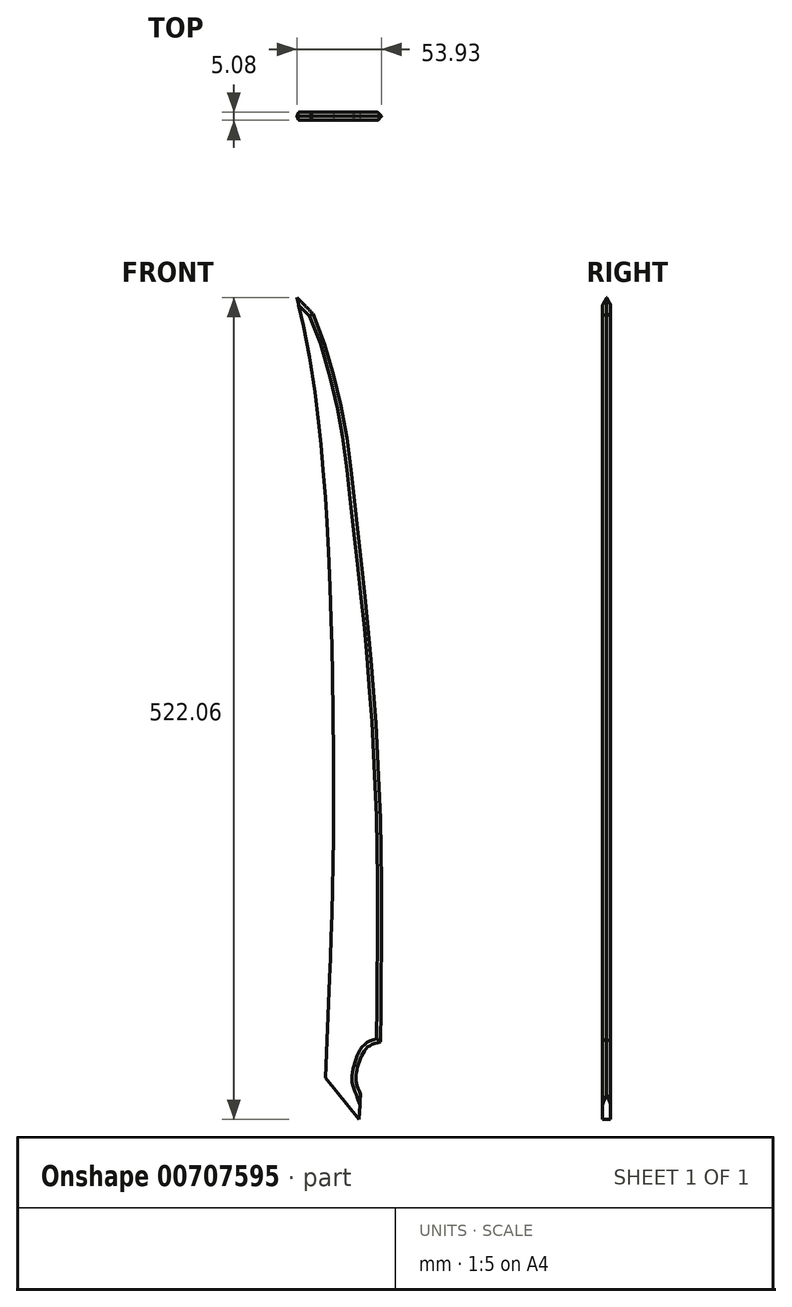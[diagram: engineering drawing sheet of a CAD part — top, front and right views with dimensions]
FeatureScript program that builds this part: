
annotation { "Feature Type Name" : "Feature", "Feature Type Description" : "" }
export const myFeature = defineFeature(function(context is Context, id is Id, definition is map)
    precondition{}
    {
        {
            var Q0;
            Q0=qCreatedBy(makeId("Front.planeOp"),FACE);
            var sketch = newSketch(context, id + "F0", { "sketchPlane" : qUnion([Q0])});
            skLineSegment(sketch, "E0", {"start": v(11.7, 8.56) * mm, "end": v(10.7, -7.18) * mm});
            skLineSegment(sketch, "E1", {"start": v(10.7, -7.18) * mm, "end": v(-10.6, 19) * mm});
            skLineSegment(sketch, "E2", {"start": v(-10.6, 19) * mm, "end": v(-7.8, 82.36) * mm});
            skFitSpline(sketch, "E3", {"points": [v(-7.8, 82.36) * mm, v(-7.24, 98.94) * mm, v(-6.59, 117.12) * mm, v(-5.83, 142.02) * mm, v(-5.45, 168.32) * mm, v(-5.52, 230.34) * mm, v(-6.26, 285.7) * mm, v(-7.2, 315.28) * mm, v(-8.95, 361.43) * mm, v(-10.4, 387.63) * mm, v(-13, 416.84) * mm, v(-15.01, 437.7) * mm, v(-21.29, 480.96) * mm, v(-27.2, 508.68) * mm, v(-28.7, 514.88) * mm], "startDerivative": vector(10.22, 308.11) * mm, "endDerivative": vector(-37.95, 155.7) * mm});
            skLineSegment(sketch, "E4", {"start": v(-28.7, 514.88) * mm, "end": v(-18.5, 504.49) * mm});
            skFitSpline(sketch, "E5", {"points": [v(-18.5, 504.49) * mm, v(-14.2, 494.72) * mm, v(-10.4, 483.17) * mm, v(-6.54, 469.9) * mm, v(-3.1, 457.05) * mm, v(-0.51, 445.6) * mm, v(1.47, 435.93) * mm, v(2.96, 426.2) * mm, v(4.35, 415.6) * mm, v(5.85, 403.15) * mm, v(7.18, 390.92) * mm, v(9.67, 369.53) * mm, v(11.56, 352.56) * mm, v(15.2, 318.42) * mm, v(18.03, 290.8) * mm, v(19.92, 265.34) * mm, v(21.72, 242.6) * mm, v(22.69, 220.79) * mm, v(23.65, 203.25) * mm, v(24.47, 178.85) * mm, v(25.08, 148.77) * mm, v(25.19, 106.94) * mm, v(24.82, 74.57) * mm, v(24.5, 42) * mm], "startDerivative": vector(138.63, -295.52) * mm, "endDerivative": vector(-5.12, -584.15) * mm});
            skFitSpline(sketch, "E6", {"points": [v(24.5, 42) * mm, v(16.7, 39) * mm, v(12.5, 33.24) * mm, v(9.61, 24.95) * mm, v(8.9, 16.91) * mm, v(10.33, 12.23) * mm, v(11.7, 8.56) * mm], "startDerivative": vector(-46.28, -12) * mm, "endDerivative": vector(10.21, -28.51) * mm});
            skFitSpline(sketch, "E7", {"points": [v(-10.6, 84.98) * mm, v(-8.5, 83) * mm, v(-6.65, 78.8) * mm, v(-5.89, 72.07) * mm, v(-5.76, 61.33) * mm, v(-5.64, 47.1) * mm, v(-5.9, 35.6) * mm, v(-6.47, 31.43) * mm, v(-6.34, 26.97) * mm, v(-4.57, 21.8) * mm, v(-2.21, 17.83) * mm, v(0, 15.05) * mm, v(2.28, 13.08) * mm, v(5.76, 11.32) * mm, v(8.69, 10.16) * mm, v(11.04, 8.9) * mm, v(12.38, 7.6) * mm, v(13.09, 5.99) * mm, v(12.89, 2.76) * mm, v(12.15, -3.9) * mm, v(11.7, -8.74) * mm, v(11.08, -13.22) * mm], "startDerivative": vector(59.9, -45.86) * mm, "endDerivative": vector(-14.62, -97.53) * mm});
            skLineSegment(sketch, "E8", {"start": v(11.08, -13.22) * mm, "end": v(11.08, -15.97) * mm});
            skLineSegment(sketch, "E9", {"start": v(11.08, -15.97) * mm, "end": v(-11.03, -15.97) * mm});
            skLineSegment(sketch, "E10", {"start": v(-11.03, -15.97) * mm, "end": v(-11.2, -13.29) * mm});
            skFitSpline(sketch, "E11", {"points": [v(-11.2, -13.29) * mm, v(-11.2, -11.84) * mm, v(-11.2, -5.52) * mm, v(-11.51, 1.49) * mm, v(-12.16, 4.66) * mm, v(-13.4, 9.05) * mm, v(-15.15, 13.55) * mm, v(-16.64, 17.33) * mm, v(-19.12, 23.61) * mm, v(-19.55, 26.56) * mm, v(-18.64, 31.28) * mm, v(-16.79, 35.33) * mm, v(-14.77, 40.57) * mm, v(-13.5, 46.17) * mm, v(-12.6, 53.4) * mm, v(-12.2, 59.96) * mm, v(-12.37, 65.97) * mm, v(-12.16, 73.91) * mm, v(-11.5, 81.04) * mm, v(-11.2, 84.64) * mm, v(-10.6, 84.98) * mm], "startDerivative": vector(-0.12, 43.3) * mm, "endDerivative": vector(35.61, 8.6) * mm});
            skFitSpline(sketch, "E12", {"points": [v(11.08, -13.22) * mm, v(15.57, -17.52) * mm, v(22.06, -24.41) * mm, v(29.6, -33.47) * mm, v(35.84, -41.56) * mm, v(40.17, -47.64) * mm, v(44.57, -55.74) * mm, v(47.94, -62.06) * mm, v(51.06, -67.51) * mm, v(52.42, -69.67) * mm, v(49.81, -81.38) * mm, v(45.5, -94.07) * mm, v(41.24, -106.63) * mm, v(36.2, -120.43) * mm, v(32.84, -130.03) * mm, v(29.35, -138.2) * mm, v(27.78, -142.23) * mm, v(23.27, -152.08) * mm, v(21.3, -154.75) * mm, v(16.02, -157.43) * mm, v(8.58, -160.03) * mm, v(4.77, -160.41) * mm, v(4.83, -154.75) * mm, v(8.26, -152.78) * mm, v(13.03, -150.3) * mm, v(16.97, -147.44) * mm, v(20.66, -141.85) * mm, v(25.37, -129.07) * mm, v(31.66, -108.36) * mm, v(36.51, -89.69) * mm, v(39.56, -77.02) * mm, v(39.75, -72.83) * mm, v(38.74, -67.42) * mm, v(35.21, -61.22) * mm, v(28.26, -50.55) * mm, v(23.02, -43.89) * mm, v(18.43, -38.21) * mm, v(13.22, -32.69) * mm, v(7.93, -27.32) * mm, v(6.6, -20.94) * mm, v(11.08, -13.22) * mm]});
            skLineSegment(sketch, "E13.bottom", {"start": v(-12.44, -13.29) * mm, "end": v(11.54, -13.29) * mm});
            skLineSegment(sketch, "E13.top", {"start": v(-12.44, -29.01) * mm, "end": v(11.54, -29.01) * mm});
            skLineSegment(sketch, "E13.left", {"start": v(-12.44, -13.29) * mm, "end": v(-12.44, -29.01) * mm});
            skLineSegment(sketch, "E13.right", {"start": v(11.54, -13.29) * mm, "end": v(11.54, -29.01) * mm});
            skLineSegment(sketch, "E14", {"start": v(0, -32.56) * mm, "end": v(0, -38.28) * mm});
            skFitSpline(sketch, "E15", {"points": [v(-10.75, -28.03) * mm, v(-9.93, -35.6) * mm, v(-9.25, -45.2) * mm, v(-8.25, -64.06) * mm, v(-7.6, -83.45) * mm, v(-7.55, -95.02) * mm, v(-7.45, -109.5) * mm, v(-7.73, -122.65) * mm, v(-8.29, -138.57) * mm, v(-9.14, -152.56) * mm, v(-9.03, -155.04) * mm], "startDerivative": vector(11.05, -94.6) * mm, "endDerivative": vector(4.37, -43.01) * mm});
            skLineSegment(sketch, "E16", {"start": v(-9.9, -153.6) * mm, "end": v(9.57, -153.6) * mm});
            skFitSpline(sketch, "E17.MirrorCS", {"points": [v(10.75, -28.03) * mm, v(9.93, -35.6) * mm, v(9.25, -45.2) * mm, v(8.25, -64.06) * mm, v(7.6, -83.45) * mm, v(7.55, -95.02) * mm, v(7.45, -109.5) * mm, v(7.73, -122.65) * mm, v(8.29, -138.57) * mm, v(9.14, -152.56) * mm, v(9.03, -155.04) * mm], "startDerivative": vector(-11.05, -94.6) * mm, "endDerivative": vector(-4.37, -43.01) * mm});
            skSolve(sketch);
        }
        {
            var Q0;
            {var subQ0=sQuery(id+"F0.wireOp",EDGE,"E3");Q0=makeQuery(id+"F0.imprint","IMPRINT",FACE,{"disambiguationData":[TD([[makeQuery(id+"F0.imprint","IMPRINT",EDGE,{"derivedFrom":subQ0}),-1.0]])]});}
            var Q1;
            {var subQ0=sQuery(id+"F0.wireOp",EDGE,"E1");Q1=makeQuery(id+"F0.imprint","IMPRINT",FACE,{"disambiguationData":[TD([[makeQuery(id+"F0.imprint","IMPRINT",EDGE,{"derivedFrom":subQ0}),-1.0]])]});}
            extrude(context, id + "F1", {"entities" : qUnion([Q0, Q1]), "depth" : 2.54 * mm, "offsetDistance" : 25.4 * mm});
        }
        {
            var Q0;
            Q0=makeQuery(id+"F1.opExtrude","CAP_FACE",FACE,{"disambiguationData":[OSD([sQuery(id+"F0.wireOp",EDGE,"E0"),sQuery(id+"F0.wireOp",EDGE,"E1"),sQuery(id+"F0.wireOp",EDGE,"E2"),sQuery(id+"F0.wireOp",EDGE,"E3"),sQuery(id+"F0.wireOp",EDGE,"E4"),sQuery(id+"F0.wireOp",EDGE,"E5"),sQuery(id+"F0.wireOp",EDGE,"E6")])],"isStart":true});
            extrude(context, id + "F2", {"entities" : qUnion([Q0]), "operationType" : NewBodyOperationType.ADD, "depth" : 2.54 * mm, "offsetDistance" : 25.4 * mm});
        }
        {
            var Q0;
            Q0=makeQuery(id+"F2.opExtrude","CAP_EDGE",EDGE,{"disambiguationData":[OSD([sQuery(id+"F0.wireOp",EDGE,"E5")])],"isStart":false});
            var Q1;
            Q1=makeQuery(id+"F1.opExtrude","CAP_EDGE",EDGE,{"disambiguationData":[OSD([sQuery(id+"F0.wireOp",EDGE,"E5")])],"isStart":false});
            var Q2;
            Q2=makeQuery(id+"F1.opExtrude","CAP_EDGE",EDGE,{"disambiguationData":[OSD([sQuery(id+"F0.wireOp",EDGE,"E4")])],"isStart":false});
            var Q3;
            Q3=makeQuery(id+"F2.opExtrude","CAP_EDGE",EDGE,{"disambiguationData":[OSD([sQuery(id+"F0.wireOp",EDGE,"E4")])],"isStart":false});
            var Q4;
            Q4=makeQuery(id+"F1.opExtrude","CAP_EDGE",EDGE,{"disambiguationData":[OSD([sQuery(id+"F0.wireOp",EDGE,"E6")])],"isStart":false});
            var Q5;
            Q5=makeQuery(id+"F2.opExtrude","CAP_EDGE",EDGE,{"disambiguationData":[OSD([sQuery(id+"F0.wireOp",EDGE,"E6")])],"isStart":false});
            chamfer(context, id + "F3", {"entities" : qUnion([Q0, Q1, Q2, Q3, Q4, Q5]), "chamferType" : ChamferType.OFFSET_ANGLE, "width" : 2.54 * mm, "oppositeDirection" : false, "angle" : 45 * degree, "tangentPropagation" : true});
        }
    });
